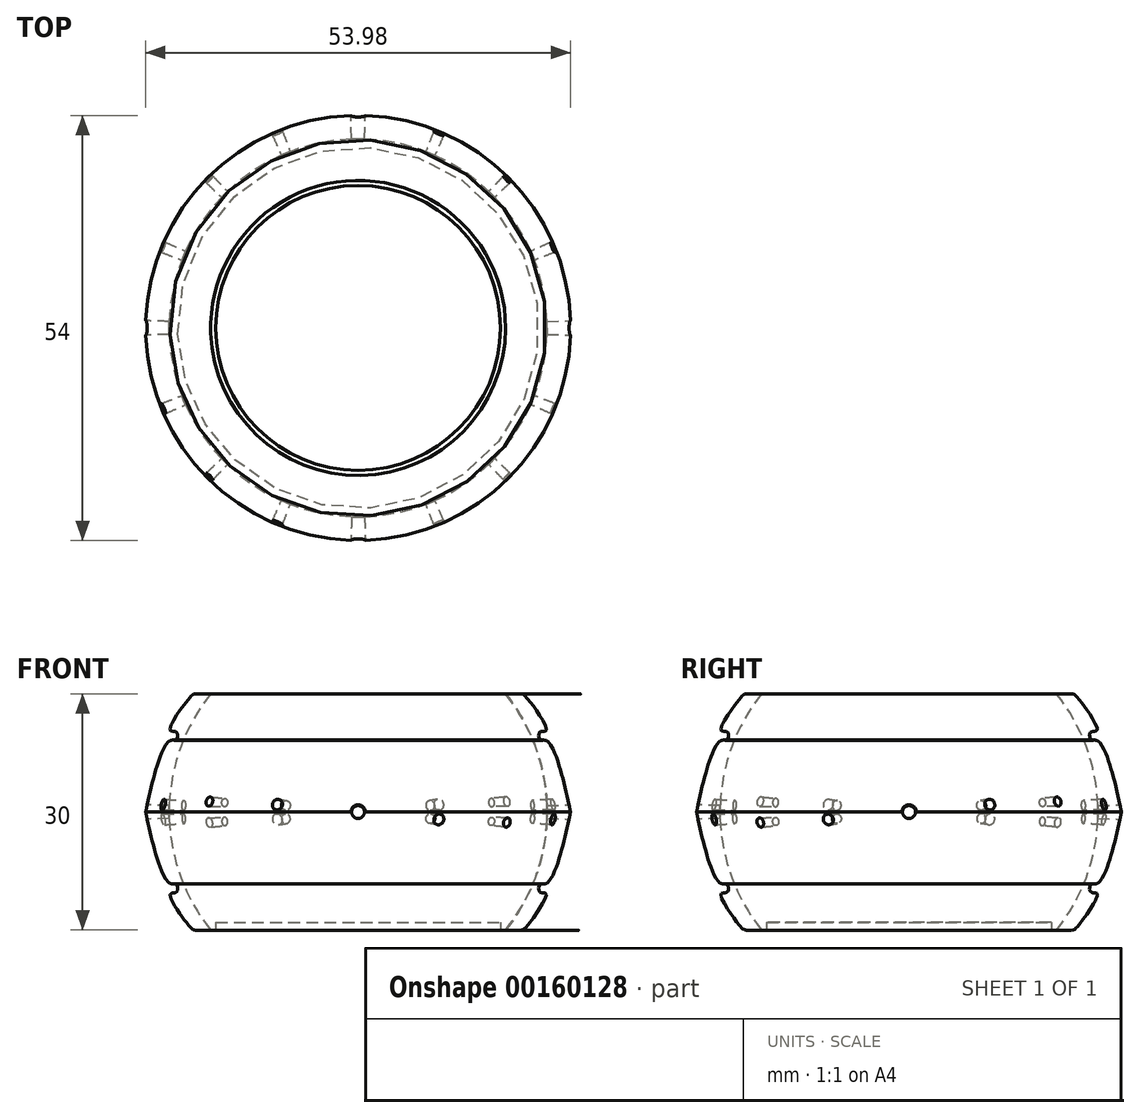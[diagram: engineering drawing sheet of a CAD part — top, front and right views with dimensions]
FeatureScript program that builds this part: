
annotation { "Feature Type Name" : "Feature", "Feature Type Description" : "" }
export const myFeature = defineFeature(function(context is Context, id is Id, definition is map)
    precondition{}
    {
        {
            var Q0;
            Q0=qCreatedBy(makeId("Top.planeOp"),FACE);
            var sketch = newSketch(context, id + "F0", { "sketchPlane" : qUnion([Q0])});
            skCircle(sketch, "E0", {"center": v(0, 0) * mm, "radius": 25 * mm});
            skLineSegment(sketch, "E1", {"start": v(-25, 0) * mm, "end": v(25, 0) * mm, "construction": true});
            skLineSegment(sketch, "E2", {"start": v(0, 25) * mm, "end": v(0, -25) * mm, "construction": true});
            skCircle(sketch, "E3", {"center": v(0, 0) * mm, "radius": 27 * mm});
            skSolve(sketch);
        }
        {
            var Q0;
            Q0=qCreatedBy(makeId("Top.planeOp"),FACE);
            var sketch = newSketch(context, id + "F1", { "sketchPlane" : qUnion([Q0])});
            skCircle(sketch, "E4.0", {"center": v(0, 0) * mm, "radius": 27 * mm, "construction": true});
            skLineSegment(sketch, "E5", {"start": v(0, 0) * mm, "end": v(-27, 0) * mm, "construction": true});
            skLineSegment(sketch, "E6", {"start": v(-27, 4.4) * mm, "end": v(-27, -4.4) * mm, "construction": true});
            skLineSegment(sketch, "E7.1.0", {"start": v(0, 0) * mm, "end": v(0, -27) * mm, "construction": true});
            skLineSegment(sketch, "E7.1.1", {"start": v(-4.4, -27) * mm, "end": v(4.4, -27) * mm, "construction": true});
            skLineSegment(sketch, "E7.2.0", {"start": v(0, 0) * mm, "end": v(27, 0) * mm, "construction": true});
            skLineSegment(sketch, "E7.2.1", {"start": v(27, -4.4) * mm, "end": v(27, 4.4) * mm, "construction": true});
            skLineSegment(sketch, "E7.3.0", {"start": v(0, 0) * mm, "end": v(0, 27) * mm, "construction": true});
            skLineSegment(sketch, "E7.3.1", {"start": v(4.4, 27) * mm, "end": v(-4.4, 27) * mm, "construction": true});
            skSolve(sketch);
        }
        {
            var Q0;
            Q0=qCreatedBy(makeId("Top.planeOp"),FACE);
            var sketch = newSketch(context, id + "F2", { "sketchPlane" : qUnion([Q0])});
            skCircle(sketch, "E8.0", {"center": v(0, 0) * mm, "radius": 27 * mm});
            skLineSegment(sketch, "E9", {"start": v(0, 0) * mm, "end": v(19.1, -19.1) * mm, "construction": true});
            skLineSegment(sketch, "E10", {"start": v(21.92, -16.26) * mm, "end": v(16.26, -21.92) * mm, "construction": true});
            skLineSegment(sketch, "E11.1.0", {"start": v(16.26, 21.92) * mm, "end": v(21.92, 16.26) * mm, "construction": true});
            skLineSegment(sketch, "E11.1.1", {"start": v(0, 0) * mm, "end": v(19.1, 19.1) * mm, "construction": true});
            skLineSegment(sketch, "E11.2.0", {"start": v(-21.92, 16.26) * mm, "end": v(-16.26, 21.92) * mm, "construction": true});
            skLineSegment(sketch, "E11.2.1", {"start": v(0, 0) * mm, "end": v(-19.1, 19.1) * mm, "construction": true});
            skLineSegment(sketch, "E11.3.0", {"start": v(-16.26, -21.92) * mm, "end": v(-21.92, -16.26) * mm, "construction": true});
            skLineSegment(sketch, "E11.3.1", {"start": v(0, 0) * mm, "end": v(-19.1, -19.1) * mm, "construction": true});
            skSolve(sketch);
        }
        {
            var Q0;
            Q0=qCreatedBy(makeId("Top.planeOp"),FACE);
            var sketch = newSketch(context, id + "F3", { "sketchPlane" : qUnion([Q0])});
            skCircle(sketch, "E12.0", {"center": v(0, 0) * mm, "radius": 27 * mm});
            skLineSegment(sketch, "E13", {"start": v(0, 0) * mm, "end": v(10.33, -24.94) * mm, "construction": true});
            skLineSegment(sketch, "E14", {"start": v(8.75, -25.6) * mm, "end": v(11.91, -24.3) * mm, "construction": true});
            skLineSegment(sketch, "E15.1.0", {"start": v(0, 0) * mm, "end": v(24.94, -10.33) * mm, "construction": true});
            skLineSegment(sketch, "E15.1.1", {"start": v(24.3, -11.91) * mm, "end": v(25.6, -8.75) * mm, "construction": true});
            skLineSegment(sketch, "E15.2.0", {"start": v(0, 0) * mm, "end": v(24.94, 10.33) * mm, "construction": true});
            skLineSegment(sketch, "E15.2.1", {"start": v(25.6, 8.75) * mm, "end": v(24.3, 11.91) * mm, "construction": true});
            skLineSegment(sketch, "E15.3.0", {"start": v(0, 0) * mm, "end": v(10.33, 24.94) * mm, "construction": true});
            skLineSegment(sketch, "E15.3.1", {"start": v(11.91, 24.3) * mm, "end": v(8.75, 25.6) * mm, "construction": true});
            skLineSegment(sketch, "E16.3.4.0", {"start": v(-8.75, 25.6) * mm, "end": v(-11.91, 24.3) * mm, "construction": true});
            skLineSegment(sketch, "E16.4.4.0", {"start": v(0, 0) * mm, "end": v(-10.33, 24.94) * mm, "construction": true});
            skLineSegment(sketch, "E16.3.5.0", {"start": v(-24.3, 11.91) * mm, "end": v(-25.6, 8.75) * mm, "construction": true});
            skLineSegment(sketch, "E16.4.5.0", {"start": v(0, 0) * mm, "end": v(-24.94, 10.33) * mm, "construction": true});
            skLineSegment(sketch, "E16.3.6.0", {"start": v(-25.6, -8.75) * mm, "end": v(-24.3, -11.91) * mm, "construction": true});
            skLineSegment(sketch, "E16.4.6.0", {"start": v(0, 0) * mm, "end": v(-24.94, -10.33) * mm, "construction": true});
            skLineSegment(sketch, "E16.3.7.0", {"start": v(-11.91, -24.3) * mm, "end": v(-8.75, -25.6) * mm, "construction": true});
            skLineSegment(sketch, "E16.4.7.0", {"start": v(0, 0) * mm, "end": v(-10.33, -24.94) * mm, "construction": true});
            skSolve(sketch);
        }
        {
            var Q0;
            Q0=qCreatedBy(makeId("Front.planeOp"),FACE);
            var sketch = newSketch(context, id + "F4", { "sketchPlane" : qUnion([Q0])});
            skLineSegment(sketch, "E17.0", {"start": v(-25, 0) * mm, "end": v(25, 0) * mm});
            skLineSegment(sketch, "E18", {"start": v(-17.86, 0) * mm, "end": v(-25, 0) * mm, "construction": true});
            skPoint(sketch, "E19", {"position": v(-18.08, 0) * mm});
            skLineSegment(sketch, "E20", {"start": v(-18.08, 15) * mm, "end": v(-17.86, 15) * mm});
            skLineSegment(sketch, "E21", {"start": v(-16.86, 14) * mm, "end": v(-16.86, -14) * mm});
            skLineSegment(sketch, "E22", {"start": v(-17.86, -15) * mm, "end": v(-18.08, -15) * mm});
            skPoint(sketch, "E23.visualSharp", {"position": v(-16.86, 15) * mm});
            skArc(sketch, "E23.filletArc", {"start": v(-16.86, 14) * mm, "mid": v(-17.16, 14.7) * mm, "end": v(-17.86, 15) * mm});
            skPoint(sketch, "E24.visualSharp", {"position": v(-16.86, -15) * mm});
            skArc(sketch, "E24.filletArc", {"start": v(-17.86, -15) * mm, "mid": v(-17.16, -14.7) * mm, "end": v(-16.86, -14) * mm});
            skLineSegment(sketch, "E25", {"start": v(0, 17.35) * mm, "end": v(0, -28.4) * mm, "construction": true});
            skFitSpline(sketch, "E26", {"points": [v(-18.08, 15) * mm, v(-19.23, 15) * mm, v(-20.08, 15) * mm, v(-20.72, 15) * mm, v(-21.23, 14.72) * mm, v(-23.9, 10.4) * mm, v(-23.1, 10.18) * mm, v(-23.1, 9.22) * mm, v(-23.95, 9.05) * mm, v(-27, 0) * mm], "startDerivative": vector(-13.01, 0) * mm, "endDerivative": vector(-9.58, -45.4) * mm});
            skFitSpline(sketch, "E27.MirrorCS", {"points": [v(-18.08, -15) * mm, v(-19.23, -15) * mm, v(-20.08, -15) * mm, v(-20.72, -15) * mm, v(-21.23, -14.72) * mm, v(-23.9, -10.4) * mm, v(-23.1, -10.18) * mm, v(-23.1, -9.22) * mm, v(-23.95, -9.05) * mm, v(-27, 0) * mm], "startDerivative": vector(-13.01, 0) * mm, "endDerivative": vector(-9.58, 45.4) * mm});
            skLineSegment(sketch, "E28", {"start": v(-18.08, -15) * mm, "end": v(0, -15) * mm});
            skLineSegment(sketch, "E29", {"start": v(0, -15) * mm, "end": v(0, -14) * mm});
            skLineSegment(sketch, "E30", {"start": v(-16.86, -14) * mm, "end": v(0, -14) * mm});
            skLineSegment(sketch, "E31", {"start": v(0, 0) * mm, "end": v(0, -15) * mm, "construction": true});
            skLineSegment(sketch, "E32", {"start": v(-16.86, -14) * mm, "end": v(-18.08, -14) * mm});
            skLineSegment(sketch, "E33", {"start": v(-18.08, -15) * mm, "end": v(-18.08, -14) * mm});
            skSolve(sketch);
        }
        {
            var Q0;
            Q0=sQuery(id+"F1.wireOp",EDGE,"E6");
            cPlane(context, id + "F5", {"entities" : qUnion([Q0]), "cplaneType" : CPlaneType.LINE_ANGLE, "offset" : 25 * mm, "angle" : 90 * degree, "width" : 150 * mm, "height" : 150 * mm});
        }
        {
            var Q0;
            Q0=qCreatedBy(id+"F5.planeOp",FACE);
            var sketch = newSketch(context, id + "F6", { "sketchPlane" : qUnion([Q0])});
            skLineSegment(sketch, "E34", {"start": v(0, 2.8) * mm, "end": v(0, -2.73) * mm, "construction": true});
            skCircle(sketch, "E35", {"center": v(0, 0) * mm, "radius": 0.93 * mm});
            skSolve(sketch);
        }
        {
            var Q0;
            Q0=makeQuery(id+"F4.imprint","IMPRINT",FACE,{"disambiguationData":[TD([[makeQuery(id+"F4.imprint","IMPRINT",EDGE,{"derivedFrom":sQuery(id+"F4.wireOp",EDGE,"E20")}),-1.0]])]});
            var Q1;
            Q1=sQuery(id+"F4.wireOp",EDGE,"E25");
            revolve(context, id + "F7", {"entities" : qUnion([Q0]), "axis" : qUnion([Q1]), "revolveType" : RevolveType.FULL});
        }
        {
            var Q0;
            Q0=makeQuery(id+"F6.imprint","IMPRINT",FACE,{"disambiguationData":[TD([[makeQuery(id+"F6.imprint","IMPRINT",EDGE,{"derivedFrom":sQuery(id+"F6.wireOp",EDGE,"E35")}),1.0]])]});
            var Q1;
            Q1=sQuery(id+"F1.wireOp",VERTEX,"E4.0.center");
            loft(context, id + "F8", {"operationType" : NewBodyOperationType.REMOVE, "sheetProfilesArray" : [{ "sheetProfileEntities" : qUnion([Q0]) }, { "sheetProfileEntities" : qUnion([Q1]) }]});
        }
        {
            var Q0;
            Q0=sQuery(id+"F1.wireOp",EDGE,"E7.3.1");
            cPlane(context, id + "F9", {"entities" : qUnion([Q0]), "cplaneType" : CPlaneType.LINE_ANGLE, "offset" : 25 * mm, "angle" : 0 * degree, "width" : 150 * mm, "height" : 150 * mm});
        }
        {
            var Q0;
            Q0=qCreatedBy(id+"F9.planeOp",FACE);
            var sketch = newSketch(context, id + "F10", { "sketchPlane" : qUnion([Q0])});
            skCircle(sketch, "E36", {"center": v(0, 0) * mm, "radius": 0.93 * mm});
            skSolve(sketch);
        }
        {
            var Q1;
            Q1=makeQuery(id+"F10.imprint","IMPRINT",FACE,{"disambiguationData":[TD([[makeQuery(id+"F10.imprint","IMPRINT",EDGE,{"derivedFrom":sQuery(id+"F10.wireOp",EDGE,"E36")}),1.0]])]});
            var Q2;
            Q2=sQuery(id+"F1.wireOp",VERTEX,"E4.0.center");
            loft(context, id + "F11", {"operationType" : NewBodyOperationType.REMOVE, "sheetProfilesArray" : [{ "sheetProfileEntities" : qUnion([Q1]) }, { "sheetProfileEntities" : qUnion([Q2]) }]});
        }
        {
            var Q0;
            Q0=sQuery(id+"F1.wireOp",EDGE,"E7.2.1");
            cPlane(context, id + "F12", {"entities" : qUnion([Q0]), "cplaneType" : CPlaneType.LINE_ANGLE, "offset" : 25 * mm, "angle" : 90 * degree, "width" : 150 * mm, "height" : 150 * mm});
        }
        {
            var Q0;
            Q0=qCreatedBy(id+"F12.planeOp",FACE);
            var sketch = newSketch(context, id + "F13", { "sketchPlane" : qUnion([Q0])});
            skCircle(sketch, "E37", {"center": v(0, 0) * mm, "radius": 0.93 * mm});
            skSolve(sketch);
        }
        {
            var Q1;
            Q1=makeQuery(id+"F13.imprint","IMPRINT",FACE,{"disambiguationData":[TD([[makeQuery(id+"F13.imprint","IMPRINT",EDGE,{"derivedFrom":sQuery(id+"F13.wireOp",EDGE,"E37")}),1.0]])]});
            var Q2;
            Q2=sQuery(id+"F1.wireOp",VERTEX,"E4.0.center");
            loft(context, id + "F14", {"operationType" : NewBodyOperationType.REMOVE, "sheetProfilesArray" : [{ "sheetProfileEntities" : qUnion([Q1]) }, { "sheetProfileEntities" : qUnion([Q2]) }]});
        }
        {
            var Q0;
            Q0=sQuery(id+"F1.wireOp",EDGE,"E7.1.1");
            cPlane(context, id + "F15", {"entities" : qUnion([Q0]), "cplaneType" : CPlaneType.LINE_ANGLE, "offset" : 25 * mm, "angle" : 0 * degree, "width" : 150 * mm, "height" : 150 * mm});
        }
        {
            var Q0;
            Q0=qCreatedBy(id+"F15.planeOp",FACE);
            var sketch = newSketch(context, id + "F16", { "sketchPlane" : qUnion([Q0])});
            skCircle(sketch, "E38", {"center": v(0, 0) * mm, "radius": 0.93 * mm});
            skSolve(sketch);
        }
        {
            var Q1;
            Q1=makeQuery(id+"F16.imprint","IMPRINT",FACE,{"disambiguationData":[TD([[makeQuery(id+"F16.imprint","IMPRINT",EDGE,{"derivedFrom":sQuery(id+"F16.wireOp",EDGE,"E38")}),1.0]])]});
            var Q2;
            Q2=sQuery(id+"F1.wireOp",VERTEX,"E4.0.center");
            loft(context, id + "F17", {"operationType" : NewBodyOperationType.REMOVE, "sheetProfilesArray" : [{ "sheetProfileEntities" : qUnion([Q1]) }, { "sheetProfileEntities" : qUnion([Q2]) }]});
        }
        {
            var Q0;
            Q0=sQuery(id+"F2.wireOp",EDGE,"E10");
            cPlane(context, id + "F18", {"entities" : qUnion([Q0]), "cplaneType" : CPlaneType.LINE_ANGLE, "offset" : 25 * mm, "angle" : 90 * degree, "width" : 150 * mm, "height" : 150 * mm});
        }
        {
            var Q0;
            Q0=qCreatedBy(id+"F18.planeOp",FACE);
            var sketch = newSketch(context, id + "F19", { "sketchPlane" : qUnion([Q0])});
            skLineSegment(sketch, "E39", {"start": v(0, 0) * mm, "end": v(0, -6.97) * mm, "construction": true});
            skCircle(sketch, "E40", {"center": v(0, -1.35) * mm, "radius": 0.6 * mm});
            skSolve(sketch);
        }
        {
            var Q1;
            Q1=makeQuery(id+"F19.imprint","IMPRINT",FACE,{"disambiguationData":[TD([[makeQuery(id+"F19.imprint","IMPRINT",EDGE,{"derivedFrom":sQuery(id+"F19.wireOp",EDGE,"E40")}),1.0]])]});
            var Q2;
            Q2=sQuery(id+"F1.wireOp",VERTEX,"E4.0.center");
            loft(context, id + "F20", {"operationType" : NewBodyOperationType.REMOVE, "sheetProfilesArray" : [{ "sheetProfileEntities" : qUnion([Q1]) }, { "sheetProfileEntities" : qUnion([Q2]) }]});
        }
        {
            var Q0;
            Q0=sQuery(id+"F2.wireOp",EDGE,"E11.3.0");
            cPlane(context, id + "F21", {"entities" : qUnion([Q0]), "cplaneType" : CPlaneType.LINE_ANGLE, "offset" : 25 * mm, "angle" : 90 * degree, "width" : 150 * mm, "height" : 150 * mm});
        }
        {
            var Q0;
            Q0=qCreatedBy(id+"F21.planeOp",FACE);
            var sketch = newSketch(context, id + "F22", { "sketchPlane" : qUnion([Q0])});
            skLineSegment(sketch, "E41", {"start": v(0, -4.31) * mm, "end": v(0, 5.75) * mm, "construction": true});
            skCircle(sketch, "E42", {"center": v(0, 1.35) * mm, "radius": 0.6 * mm});
            skSolve(sketch);
        }
        {
            var Q1;
            Q1=makeQuery(id+"F22.imprint","IMPRINT",FACE,{"disambiguationData":[TD([[makeQuery(id+"F22.imprint","IMPRINT",EDGE,{"derivedFrom":sQuery(id+"F22.wireOp",EDGE,"E42")}),1.0]])]});
            var Q2;
            Q2=sQuery(id+"F1.wireOp",VERTEX,"E4.0.center");
            loft(context, id + "F23", {"operationType" : NewBodyOperationType.REMOVE, "sheetProfilesArray" : [{ "sheetProfileEntities" : qUnion([Q1]) }, { "sheetProfileEntities" : qUnion([Q2]) }]});
        }
        {
            var Q0;
            Q0=sQuery(id+"F2.wireOp",EDGE,"E11.2.0");
            cPlane(context, id + "F24", {"entities" : qUnion([Q0]), "cplaneType" : CPlaneType.LINE_ANGLE, "offset" : 25 * mm, "angle" : 90 * degree, "width" : 150 * mm, "height" : 150 * mm});
        }
        {
            var Q0;
            Q0=qCreatedBy(id+"F24.planeOp",FACE);
            var sketch = newSketch(context, id + "F25", { "sketchPlane" : qUnion([Q0])});
            skLineSegment(sketch, "E43", {"start": v(0, 5.18) * mm, "end": v(0, -5.52) * mm, "construction": true});
            skCircle(sketch, "E44", {"center": v(0, -1.35) * mm, "radius": 0.6 * mm});
            skSolve(sketch);
        }
        {
            var Q1;
            Q1=makeQuery(id+"F25.imprint","IMPRINT",FACE,{"disambiguationData":[TD([[makeQuery(id+"F25.imprint","IMPRINT",EDGE,{"derivedFrom":sQuery(id+"F25.wireOp",EDGE,"E44")}),1.0]])]});
            var Q2;
            Q2=sQuery(id+"F1.wireOp",VERTEX,"E4.0.center");
            loft(context, id + "F26", {"operationType" : NewBodyOperationType.REMOVE, "sheetProfilesArray" : [{ "sheetProfileEntities" : qUnion([Q1]) }, { "sheetProfileEntities" : qUnion([Q2]) }]});
        }
        {
            var Q0;
            Q0=sQuery(id+"F2.wireOp",EDGE,"E11.1.0");
            cPlane(context, id + "F27", {"entities" : qUnion([Q0]), "cplaneType" : CPlaneType.LINE_ANGLE, "offset" : 25 * mm, "angle" : 90 * degree, "width" : 150 * mm, "height" : 150 * mm});
        }
        {
            var Q0;
            Q0=qCreatedBy(id+"F27.planeOp",FACE);
            var sketch = newSketch(context, id + "F28", { "sketchPlane" : qUnion([Q0])});
            skLineSegment(sketch, "E45", {"start": v(0, -3.41) * mm, "end": v(0, 4.01) * mm, "construction": true});
            skCircle(sketch, "E46", {"center": v(0, 1.35) * mm, "radius": 0.6 * mm});
            skSolve(sketch);
        }
        {
            var Q1;
            Q1=makeQuery(id+"F28.imprint","IMPRINT",FACE,{"disambiguationData":[TD([[makeQuery(id+"F28.imprint","IMPRINT",EDGE,{"derivedFrom":sQuery(id+"F28.wireOp",EDGE,"E46")}),1.0]])]});
            var Q2;
            Q2=sQuery(id+"F1.wireOp",VERTEX,"E4.0.center");
            loft(context, id + "F29", {"operationType" : NewBodyOperationType.REMOVE, "sheetProfilesArray" : [{ "sheetProfileEntities" : qUnion([Q1]) }, { "sheetProfileEntities" : qUnion([Q2]) }]});
        }
        {
            var Q0;
            Q0=sQuery(id+"F3.wireOp",EDGE,"E14");
            cPlane(context, id + "F30", {"entities" : qUnion([Q0]), "cplaneType" : CPlaneType.LINE_ANGLE, "offset" : 25 * mm, "angle" : 0 * degree, "width" : 150 * mm, "height" : 150 * mm});
        }
        {
            var Q0;
            Q0=qCreatedBy(id+"F30.planeOp",FACE);
            var sketch = newSketch(context, id + "F31", { "sketchPlane" : qUnion([Q0])});
            skLineSegment(sketch, "E47", {"start": v(0, 1.86) * mm, "end": v(0, -3.93) * mm, "construction": true});
            skCircle(sketch, "E48", {"center": v(0, -0.95) * mm, "radius": 0.7 * mm});
            skSolve(sketch);
        }
        {
            var Q1;
            Q1=makeQuery(id+"F31.imprint","IMPRINT",FACE,{"disambiguationData":[TD([[makeQuery(id+"F31.imprint","IMPRINT",EDGE,{"derivedFrom":sQuery(id+"F31.wireOp",EDGE,"E48")}),1.0]])]});
            var Q2;
            Q2=sQuery(id+"F3.wireOp",VERTEX,"E12.0.center");
            loft(context, id + "F32", {"operationType" : NewBodyOperationType.REMOVE, "sheetProfilesArray" : [{ "sheetProfileEntities" : qUnion([Q1]) }, { "sheetProfileEntities" : qUnion([Q2]) }]});
        }
        {
            var Q0;
            Q0=sQuery(id+"F3.wireOp",EDGE,"E16.3.7.0");
            cPlane(context, id + "F33", {"entities" : qUnion([Q0]), "cplaneType" : CPlaneType.LINE_ANGLE, "offset" : 25 * mm, "angle" : 0 * degree, "width" : 150 * mm, "height" : 150 * mm});
        }
        {
            var Q0;
            Q0=qCreatedBy(id+"F33.planeOp",FACE);
            var sketch = newSketch(context, id + "F34", { "sketchPlane" : qUnion([Q0])});
            skLineSegment(sketch, "E49", {"start": v(0, -5.3) * mm, "end": v(0, 5.97) * mm, "construction": true});
            skCircle(sketch, "E50", {"center": v(0, 0.95) * mm, "radius": 0.7 * mm});
            skSolve(sketch);
        }
        {
            var Q1;
            Q1=makeQuery(id+"F34.imprint","IMPRINT",FACE,{"disambiguationData":[TD([[makeQuery(id+"F34.imprint","IMPRINT",EDGE,{"derivedFrom":sQuery(id+"F34.wireOp",EDGE,"E50")}),1.0]])]});
            var Q2;
            Q2=sQuery(id+"F3.wireOp",VERTEX,"E12.0.center");
            loft(context, id + "F35", {"operationType" : NewBodyOperationType.REMOVE, "sheetProfilesArray" : [{ "sheetProfileEntities" : qUnion([Q1]) }, { "sheetProfileEntities" : qUnion([Q2]) }]});
        }
        {
            var Q0;
            Q0=sQuery(id+"F3.wireOp",EDGE,"E16.3.6.0");
            cPlane(context, id + "F36", {"entities" : qUnion([Q0]), "cplaneType" : CPlaneType.LINE_ANGLE, "offset" : 25 * mm, "angle" : 90 * degree, "width" : 150 * mm, "height" : 150 * mm});
        }
        {
            var Q0;
            Q0=qCreatedBy(id+"F36.planeOp",FACE);
            var sketch = newSketch(context, id + "F37", { "sketchPlane" : qUnion([Q0])});
            skLineSegment(sketch, "E51", {"start": v(0, -0.9) * mm, "end": v(0, 3) * mm, "construction": true});
            skCircle(sketch, "E52", {"center": v(0, 0.95) * mm, "radius": 0.7 * mm});
            skSolve(sketch);
        }
        {
            var Q1;
            Q1=makeQuery(id+"F37.imprint","IMPRINT",FACE,{"disambiguationData":[TD([[makeQuery(id+"F37.imprint","IMPRINT",EDGE,{"derivedFrom":sQuery(id+"F37.wireOp",EDGE,"E52")}),1.0]])]});
            var Q2;
            Q2=sQuery(id+"F3.wireOp",VERTEX,"E12.0.center");
            loft(context, id + "F38", {"operationType" : NewBodyOperationType.REMOVE, "sheetProfilesArray" : [{ "sheetProfileEntities" : qUnion([Q1]) }, { "sheetProfileEntities" : qUnion([Q2]) }]});
        }
        {
            var Q0;
            Q0=sQuery(id+"F3.wireOp",EDGE,"E16.3.5.0");
            cPlane(context, id + "F39", {"entities" : qUnion([Q0]), "cplaneType" : CPlaneType.LINE_ANGLE, "offset" : 25 * mm, "angle" : 90 * degree, "width" : 150 * mm, "height" : 150 * mm});
        }
        {
            var Q0;
            Q0=qCreatedBy(id+"F39.planeOp",FACE);
            var sketch = newSketch(context, id + "F40", { "sketchPlane" : qUnion([Q0])});
            skLineSegment(sketch, "E53", {"start": v(0, 0) * mm, "end": v(0, -1.9) * mm, "construction": true});
            skCircle(sketch, "E54", {"center": v(0, -0.95) * mm, "radius": 0.7 * mm});
            skSolve(sketch);
        }
        {
            var Q1;
            Q1=makeQuery(id+"F40.imprint","IMPRINT",FACE,{"disambiguationData":[TD([[makeQuery(id+"F40.imprint","IMPRINT",EDGE,{"derivedFrom":sQuery(id+"F40.wireOp",EDGE,"E54")}),1.0]])]});
            var Q2;
            Q2=sQuery(id+"F3.wireOp",VERTEX,"E12.0.center");
            loft(context, id + "F41", {"operationType" : NewBodyOperationType.REMOVE, "sheetProfilesArray" : [{ "sheetProfileEntities" : qUnion([Q1]) }, { "sheetProfileEntities" : qUnion([Q2]) }]});
        }
        {
            var Q0;
            Q0=sQuery(id+"F3.wireOp",EDGE,"E16.3.4.0");
            cPlane(context, id + "F42", {"entities" : qUnion([Q0]), "cplaneType" : CPlaneType.LINE_ANGLE, "offset" : 25 * mm, "angle" : 0 * degree, "width" : 150 * mm, "height" : 150 * mm});
        }
        {
            var Q0;
            Q0=qCreatedBy(id+"F42.planeOp",FACE);
            var sketch = newSketch(context, id + "F43", { "sketchPlane" : qUnion([Q0])});
            skLineSegment(sketch, "E55", {"start": v(0, 0) * mm, "end": v(0, -3.77) * mm, "construction": true});
            skCircle(sketch, "E56", {"center": v(0, -0.95) * mm, "radius": 0.7 * mm});
            skSolve(sketch);
        }
        {
            var Q1;
            Q1=sQuery(id+"F3.wireOp",VERTEX,"E12.0.center");
            var Q2;
            Q2=makeQuery(id+"F43.imprint","IMPRINT",FACE,{"disambiguationData":[TD([[makeQuery(id+"F43.imprint","IMPRINT",EDGE,{"derivedFrom":sQuery(id+"F43.wireOp",EDGE,"E56")}),1.0]])]});
            loft(context, id + "F44", {"operationType" : NewBodyOperationType.REMOVE, "sheetProfilesArray" : [{ "sheetProfileEntities" : qUnion([Q1]) }, { "sheetProfileEntities" : qUnion([Q2]) }]});
        }
        {
            var Q0;
            Q0=sQuery(id+"F3.wireOp",EDGE,"E15.3.1");
            cPlane(context, id + "F45", {"entities" : qUnion([Q0]), "cplaneType" : CPlaneType.LINE_ANGLE, "offset" : 25 * mm, "angle" : 0 * degree, "width" : 150 * mm, "height" : 150 * mm});
        }
        {
            var Q0;
            Q0=qCreatedBy(id+"F45.planeOp",FACE);
            var sketch = newSketch(context, id + "F46", { "sketchPlane" : qUnion([Q0])});
            skLineSegment(sketch, "E57", {"start": v(0, 0) * mm, "end": v(0, 2.17) * mm, "construction": true});
            skCircle(sketch, "E58", {"center": v(0, 0.95) * mm, "radius": 0.7 * mm});
            skSolve(sketch);
        }
        {
            var Q1;
            Q1=makeQuery(id+"F46.imprint","IMPRINT",FACE,{"disambiguationData":[TD([[makeQuery(id+"F46.imprint","IMPRINT",EDGE,{"derivedFrom":sQuery(id+"F46.wireOp",EDGE,"E58")}),1.0]])]});
            var Q2;
            Q2=sQuery(id+"F3.wireOp",VERTEX,"E12.0.center");
            loft(context, id + "F47", {"operationType" : NewBodyOperationType.REMOVE, "sheetProfilesArray" : [{ "sheetProfileEntities" : qUnion([Q1]) }, { "sheetProfileEntities" : qUnion([Q2]) }]});
        }
        {
            var Q0;
            Q0=sQuery(id+"F3.wireOp",EDGE,"E15.2.1");
            cPlane(context, id + "F48", {"entities" : qUnion([Q0]), "cplaneType" : CPlaneType.LINE_ANGLE, "offset" : 25 * mm, "angle" : 90 * degree, "width" : 150 * mm, "height" : 150 * mm});
        }
        {
            var Q0;
            Q0=qCreatedBy(id+"F48.planeOp",FACE);
            var sketch = newSketch(context, id + "F49", { "sketchPlane" : qUnion([Q0])});
            skLineSegment(sketch, "E59", {"start": v(0, 0) * mm, "end": v(0, 3.06) * mm, "construction": true});
            skCircle(sketch, "E60", {"center": v(0, 0.95) * mm, "radius": 0.7 * mm});
            skSolve(sketch);
        }
        {
            var Q1;
            Q1=makeQuery(id+"F49.imprint","IMPRINT",FACE,{"disambiguationData":[TD([[makeQuery(id+"F49.imprint","IMPRINT",EDGE,{"derivedFrom":sQuery(id+"F49.wireOp",EDGE,"E60")}),1.0]])]});
            var Q2;
            Q2=sQuery(id+"F3.wireOp",VERTEX,"E12.0.center");
            loft(context, id + "F50", {"operationType" : NewBodyOperationType.REMOVE, "sheetProfilesArray" : [{ "sheetProfileEntities" : qUnion([Q1]) }, { "sheetProfileEntities" : qUnion([Q2]) }]});
        }
        {
            var Q0;
            Q0=sQuery(id+"F3.wireOp",EDGE,"E15.1.1");
            cPlane(context, id + "F51", {"entities" : qUnion([Q0]), "cplaneType" : CPlaneType.LINE_ANGLE, "offset" : 25 * mm, "angle" : 90 * degree, "width" : 150 * mm, "height" : 150 * mm});
        }
        {
            var Q0;
            Q0=qCreatedBy(id+"F51.planeOp",FACE);
            var sketch = newSketch(context, id + "F52", { "sketchPlane" : qUnion([Q0])});
            skLineSegment(sketch, "E61", {"start": v(0, 0) * mm, "end": v(0, -1.7) * mm, "construction": true});
            skCircle(sketch, "E62", {"center": v(0, -0.95) * mm, "radius": 0.7 * mm});
            skSolve(sketch);
        }
        {
            var Q1;
            Q1=makeQuery(id+"F52.imprint","IMPRINT",FACE,{"disambiguationData":[TD([[makeQuery(id+"F52.imprint","IMPRINT",EDGE,{"derivedFrom":sQuery(id+"F52.wireOp",EDGE,"E62")}),1.0]])]});
            var Q2;
            Q2=sQuery(id+"F3.wireOp",VERTEX,"E12.0.center");
            loft(context, id + "F53", {"operationType" : NewBodyOperationType.REMOVE, "sheetProfilesArray" : [{ "sheetProfileEntities" : qUnion([Q1]) }, { "sheetProfileEntities" : qUnion([Q2]) }]});
        }
        {
            var Q0;
            Q0=qCreatedBy(makeId("Front.planeOp"),FACE);
            var sketch = newSketch(context, id + "F54", { "sketchPlane" : qUnion([Q0])});
            skCircle(sketch, "E63", {"center": v(0, 0) * mm, "radius": 24 * mm});
            skLineSegment(sketch, "E64", {"start": v(0, 24) * mm, "end": v(0, -24) * mm});
            skSolve(sketch);
        }
        {
            var Q0;
            {var subQ0=sQuery(id+"F54.wireOp",EDGE,"E64");Q0=makeQuery(id+"F54.imprint","IMPRINT",FACE,{"disambiguationData":[TD([[makeQuery(id+"F54.imprint","IMPRINT",EDGE,{"derivedFrom":subQ0}),-1.0]])]});}
            var Q1;
            Q1=sQuery(id+"F54.wireOp",EDGE,"E64");
            revolve(context, id + "F55", {"operationType" : NewBodyOperationType.REMOVE, "entities" : qUnion([Q0]), "axis" : qUnion([Q1]), "revolveType" : RevolveType.FULL, "oppositeDirection" : true});
        }
        {
            var Q0;
            {var subQ0=sQuery(id+"F4.wireOp",EDGE,"E24.filletArc");Q0=makeQuery(id+"F4.imprint","IMPRINT",FACE,{"disambiguationData":[TD([[makeQuery(id+"F4.imprint","IMPRINT",EDGE,{"derivedFrom":subQ0}),1.0]])]});}
            var Q1;
            {var subQ0=sQuery(id+"F4.wireOp",EDGE,"E24.filletArc");Q1=makeQuery(id+"F4.imprint","IMPRINT",FACE,{"disambiguationData":[TD([[makeQuery(id+"F4.imprint","IMPRINT",EDGE,{"derivedFrom":subQ0}),-1.0]])]});}
            var Q2;
            Q2=sQuery(id+"F4.wireOp",EDGE,"E29");
            revolve(context, id + "F56", {"operationType" : NewBodyOperationType.ADD, "entities" : qUnion([Q0, Q1]), "axis" : qUnion([Q2]), "revolveType" : RevolveType.FULL});
        }
    });
